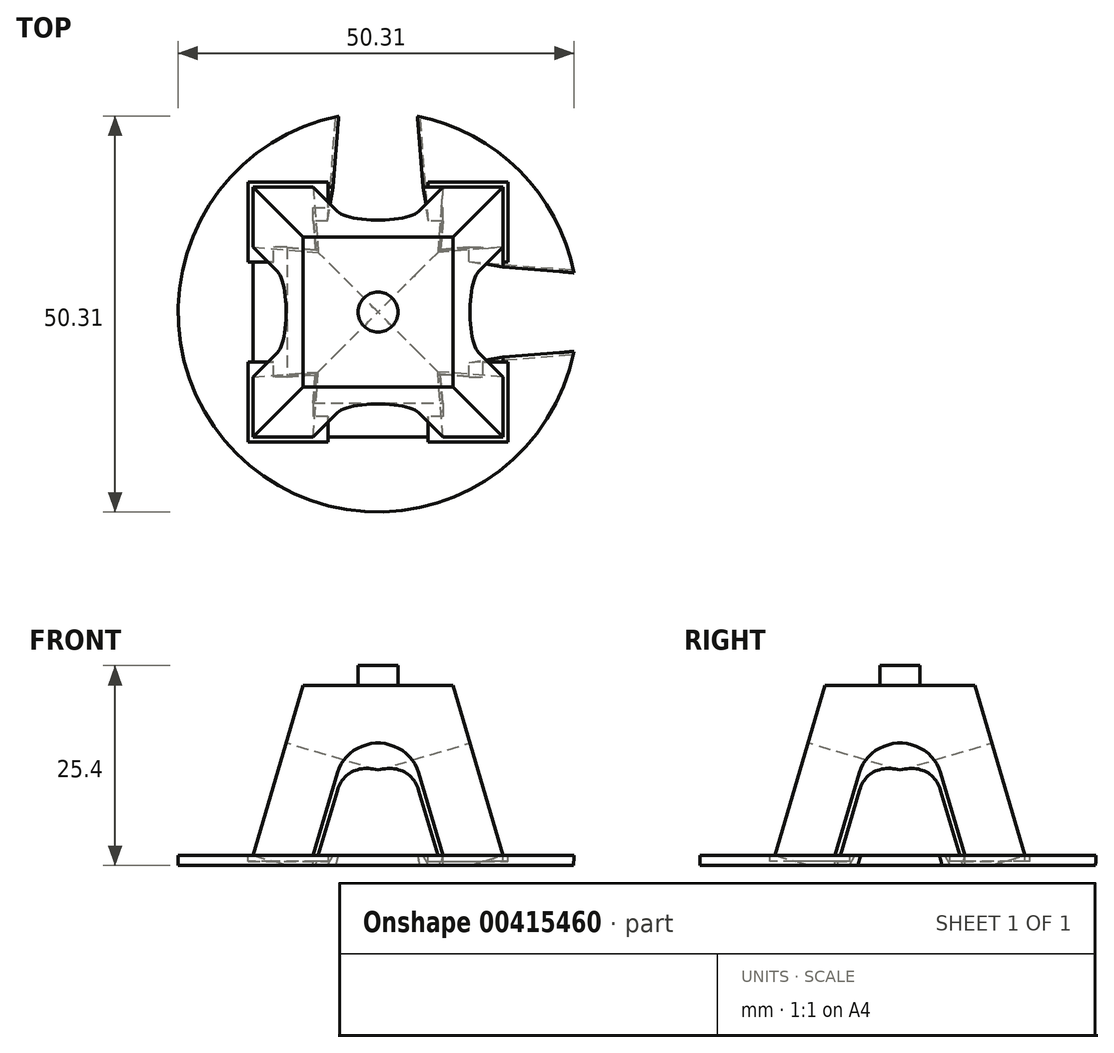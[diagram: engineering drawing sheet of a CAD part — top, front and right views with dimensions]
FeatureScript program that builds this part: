
annotation { "Feature Type Name" : "Feature", "Feature Type Description" : "" }
export const myFeature = defineFeature(function(context is Context, id is Id, definition is map)
    precondition{}
    {
        {
            var Q0;
            Q0=qCreatedBy(makeId("Top.planeOp"),FACE);
            var sketch = newSketch(context, id + "F0", { "sketchPlane" : qUnion([Q0])});
            skCircle(sketch, "E0", {"center": v(0, 0) * mm, "radius": 25.4 * mm});
            skSolve(sketch);
        }
        {
            var Q0;
            Q0=makeQuery(id+"F0.imprint","IMPRINT",FACE,{"disambiguationData":[TD([[makeQuery(id+"F0.imprint","IMPRINT",EDGE,{"derivedFrom":sQuery(id+"F0.wireOp",EDGE,"E0")}),1.0]])]});
            extrude(context, id + "F1", {"entities" : qUnion([Q0]), "oppositeDirection" : true, "depth" : 1.27 * mm});
        }
        {
            var Q0;
            Q0=qCreatedBy(makeId("Top.planeOp"),FACE);
            var sketch = newSketch(context, id + "F2", { "sketchPlane" : qUnion([Q0])});
            skLineSegment(sketch, "E1.bottom", {"start": v(-15.87, 15.88) * mm, "end": v(15.88, 15.88) * mm});
            skLineSegment(sketch, "E1.top", {"start": v(-15.88, -15.87) * mm, "end": v(15.87, -15.87) * mm});
            skLineSegment(sketch, "E1.left", {"start": v(-15.87, 15.88) * mm, "end": v(-15.88, -15.87) * mm});
            skLineSegment(sketch, "E1.right", {"start": v(15.88, 15.88) * mm, "end": v(15.87, -15.87) * mm});
            skPoint(sketch, "E1.middle", {"position": v(0, 0) * mm});
            skSolve(sketch);
        }
        {
            var Q0;
            Q0=qCreatedBy(makeId("Top.planeOp"),FACE);
            cPlane(context, id + "F3", {"entities" : qUnion([Q0]), "cplaneType" : CPlaneType.OFFSET, "offset" : 21.59 * mm, "width" : 152.4 * mm, "height" : 152.4 * mm});
        }
        {
            var Q0;
            Q0=qCreatedBy(id+"F3.planeOp",FACE);
            var sketch = newSketch(context, id + "F4", { "sketchPlane" : qUnion([Q0])});
            skLineSegment(sketch, "E2.bottom", {"start": v(-9.52, 9.53) * mm, "end": v(9.53, 9.53) * mm});
            skLineSegment(sketch, "E2.top", {"start": v(-9.53, -9.52) * mm, "end": v(9.52, -9.52) * mm});
            skLineSegment(sketch, "E2.left", {"start": v(-9.52, 9.53) * mm, "end": v(-9.53, -9.52) * mm});
            skLineSegment(sketch, "E2.right", {"start": v(9.53, 9.53) * mm, "end": v(9.53, -9.52) * mm});
            skPoint(sketch, "E2.middle", {"position": v(0, 0) * mm});
            skSolve(sketch);
        }
        {
            var Q1;
            Q1=makeQuery(id+"F2.imprint","IMPRINT",FACE,{"disambiguationData":[TD([[makeQuery(id+"F2.imprint","IMPRINT",EDGE,{"derivedFrom":sQuery(id+"F2.wireOp",EDGE,"E1.bottom")}),-1.0]])]});
            var Q2;
            Q2=makeQuery(id+"F4.imprint","IMPRINT",FACE,{"disambiguationData":[TD([[makeQuery(id+"F4.imprint","IMPRINT",EDGE,{"derivedFrom":sQuery(id+"F4.wireOp",EDGE,"E2.bottom")}),-1.0]])]});
            loft(context, id + "F5", {"sheetProfilesArray" : [{ "sheetProfileEntities" : qUnion([Q1]) }, { "sheetProfileEntities" : qUnion([Q2]) }]});
        }
        {
            var Q0;
            Q0=makeQuery(id+"F5.opLoft","SWEPT_FACE",FACE,{"disambiguationData":[OSD([sQuery(id+"F2.wireOp",EDGE,"E1.top"),sQuery(id+"F2.wireOp",EDGE,"E1.left"),sQuery(id+"F2.wireOp",EDGE,"E1.right"),sQuery(id+"F4.wireOp",EDGE,"E2.top"),sQuery(id+"F4.wireOp",EDGE,"E2.left"),sQuery(id+"F4.wireOp",EDGE,"E2.right")])]});
            var sketch = newSketch(context, id + "F6", { "sketchPlane" : qUnion([Q0])});
            skLineSegment(sketch, "E3.0.0", {"start": v(15.87, -4.48) * mm, "end": v(9.53, 18.03) * mm});
            skLineSegment(sketch, "E3.0.1", {"start": v(9.53, 18.03) * mm, "end": v(-9.53, 18.03) * mm});
            skLineSegment(sketch, "E3.0.2", {"start": v(-9.53, 18.03) * mm, "end": v(-15.88, -4.48) * mm});
            skLineSegment(sketch, "E3.0.3", {"start": v(-15.88, -4.48) * mm, "end": v(15.87, -4.48) * mm});
            skLineSegment(sketch, "E4", {"start": v(-8.26, -4.48) * mm, "end": v(-5.16, 6.5) * mm});
            skLineSegment(sketch, "E5", {"start": v(8.25, -4.48) * mm, "end": v(5.16, 6.5) * mm});
            skArc(sketch, "E6", {"start": v(5.16, 6.5) * mm, "mid": v(0, 10.4) * mm, "end": v(-5.16, 6.5) * mm});
            skLineSegment(sketch, "E7", {"start": v(-5.16, 6.5) * mm, "end": v(-1.9, 18.03) * mm, "construction": true});
            skLineSegment(sketch, "E8", {"start": v(5.16, 6.5) * mm, "end": v(1.9, 18.03) * mm, "construction": true});
            skSolve(sketch);
        }
        {
            var Q0;
            Q0=makeQuery(id+"F5.opLoft","SWEPT_FACE",FACE,{"disambiguationData":[OSD([sQuery(id+"F2.wireOp",EDGE,"E1.bottom"),sQuery(id+"F2.wireOp",EDGE,"E1.top"),sQuery(id+"F2.wireOp",EDGE,"E1.right"),sQuery(id+"F4.wireOp",EDGE,"E2.bottom"),sQuery(id+"F4.wireOp",EDGE,"E2.top"),sQuery(id+"F4.wireOp",EDGE,"E2.right")])]});
            var sketch = newSketch(context, id + "F7", { "sketchPlane" : qUnion([Q0])});
            skLineSegment(sketch, "E9.0.0", {"start": v(15.88, -4.48) * mm, "end": v(9.52, 18.03) * mm});
            skLineSegment(sketch, "E9.0.1", {"start": v(-9.52, 18.03) * mm, "end": v(9.53, 18.03) * mm});
            skLineSegment(sketch, "E9.0.2", {"start": v(-9.52, 18.03) * mm, "end": v(-15.87, -4.48) * mm});
            skLineSegment(sketch, "E9.0.3", {"start": v(-15.87, -4.48) * mm, "end": v(15.88, -4.48) * mm});
            skLineSegment(sketch, "E10", {"start": v(-8.25, -4.48) * mm, "end": v(-5.16, 6.5) * mm});
            skLineSegment(sketch, "E11", {"start": v(8.26, -4.48) * mm, "end": v(5.16, 6.5) * mm});
            skArc(sketch, "E12", {"start": v(5.16, 6.5) * mm, "mid": v(0, 10.4) * mm, "end": v(-5.16, 6.5) * mm});
            skSolve(sketch);
        }
        {
            var Q0;
            Q0=makeQuery(id+"F5.opLoft","SWEPT_FACE",FACE,{"disambiguationData":[OSD([sQuery(id+"F2.wireOp",EDGE,"E1.bottom"),sQuery(id+"F2.wireOp",EDGE,"E1.left"),sQuery(id+"F2.wireOp",EDGE,"E1.right"),sQuery(id+"F4.wireOp",EDGE,"E2.bottom"),sQuery(id+"F4.wireOp",EDGE,"E2.left"),sQuery(id+"F4.wireOp",EDGE,"E2.right")])]});
            var sketch = newSketch(context, id + "F8", { "sketchPlane" : qUnion([Q0])});
            skLineSegment(sketch, "E13.0.0", {"start": v(-9.53, 18.03) * mm, "end": v(9.52, 18.03) * mm});
            skLineSegment(sketch, "E13.0.1", {"start": v(-9.53, 18.03) * mm, "end": v(-15.88, -4.48) * mm});
            skLineSegment(sketch, "E13.0.2", {"start": v(-15.88, -4.48) * mm, "end": v(15.87, -4.48) * mm});
            skLineSegment(sketch, "E13.0.3", {"start": v(15.87, -4.48) * mm, "end": v(9.53, 18.03) * mm});
            skLineSegment(sketch, "E14", {"start": v(-8.26, -4.48) * mm, "end": v(-5.16, 6.5) * mm});
            skLineSegment(sketch, "E15", {"start": v(8.25, -4.48) * mm, "end": v(5.16, 6.5) * mm});
            skArc(sketch, "E16", {"start": v(5.16, 6.5) * mm, "mid": v(0, 10.4) * mm, "end": v(-5.16, 6.5) * mm});
            skSolve(sketch);
        }
        {
            var Q0;
            Q0=makeQuery(id+"F5.opLoft","SWEPT_FACE",FACE,{"disambiguationData":[OSD([sQuery(id+"F2.wireOp",EDGE,"E1.bottom"),sQuery(id+"F2.wireOp",EDGE,"E1.top"),sQuery(id+"F2.wireOp",EDGE,"E1.left"),sQuery(id+"F4.wireOp",EDGE,"E2.bottom"),sQuery(id+"F4.wireOp",EDGE,"E2.top"),sQuery(id+"F4.wireOp",EDGE,"E2.left")])]});
            var sketch = newSketch(context, id + "F9", { "sketchPlane" : qUnion([Q0])});
            skLineSegment(sketch, "E17.0.0", {"start": v(15.88, -4.48) * mm, "end": v(9.53, 18.03) * mm});
            skLineSegment(sketch, "E17.0.1", {"start": v(9.53, 18.03) * mm, "end": v(-9.52, 18.03) * mm});
            skLineSegment(sketch, "E17.0.2", {"start": v(-9.53, 18.03) * mm, "end": v(-15.87, -4.48) * mm});
            skLineSegment(sketch, "E17.0.3", {"start": v(-15.87, -4.48) * mm, "end": v(15.88, -4.48) * mm});
            skLineSegment(sketch, "E18", {"start": v(-8.25, -4.48) * mm, "end": v(-5.16, 6.5) * mm});
            skLineSegment(sketch, "E19", {"start": v(8.26, -4.48) * mm, "end": v(5.16, 6.5) * mm});
            skArc(sketch, "E20", {"start": v(5.16, 6.5) * mm, "mid": v(0, 10.4) * mm, "end": v(-5.16, 6.5) * mm});
            skSolve(sketch);
        }
        {
            var Q0;
            {var subQ0=sQuery(id+"F9.wireOp",EDGE,"E18");Q0=makeQuery(id+"F9.imprint","IMPRINT",FACE,{"disambiguationData":[TD([[makeQuery(id+"F9.imprint","IMPRINT",EDGE,{"derivedFrom":subQ0}),-1.0]])]});}
            extrude(context, id + "F10", {"entities" : qUnion([Q0]), "operationType" : NewBodyOperationType.REMOVE, "oppositeDirection" : true, "depth" : 74.42 * mm});
        }
        {
            var Q0;
            {var subQ0=sQuery(id+"F6.wireOp",EDGE,"E4");Q0=makeQuery(id+"F6.imprint","IMPRINT",FACE,{"disambiguationData":[TD([[makeQuery(id+"F6.imprint","IMPRINT",EDGE,{"derivedFrom":subQ0}),-1.0]])]});}
            extrude(context, id + "F11", {"entities" : qUnion([Q0]), "operationType" : NewBodyOperationType.REMOVE, "oppositeDirection" : true, "depth" : 67.8 * mm});
        }
        {
            var Q0;
            {var subQ0=sQuery(id+"F7.wireOp",EDGE,"E10");Q0=makeQuery(id+"F7.imprint","IMPRINT",FACE,{"disambiguationData":[TD([[makeQuery(id+"F7.imprint","IMPRINT",EDGE,{"derivedFrom":subQ0}),-1.0]])]});}
            extrude(context, id + "F12", {"entities" : qUnion([Q0]), "operationType" : NewBodyOperationType.REMOVE, "oppositeDirection" : true, "depth" : 25.4 * mm});
        }
        {
            var Q0;
            {var subQ0=sQuery(id+"F8.wireOp",EDGE,"E14");Q0=makeQuery(id+"F8.imprint","IMPRINT",FACE,{"disambiguationData":[TD([[makeQuery(id+"F8.imprint","IMPRINT",EDGE,{"derivedFrom":subQ0}),-1.0]])]});}
            extrude(context, id + "F13", {"entities" : qUnion([Q0]), "operationType" : NewBodyOperationType.REMOVE, "oppositeDirection" : true, "depth" : 25.4 * mm});
        }
        {
            var Q0;
            Q0=makeQuery(id+"F1.opExtrude","CAP_FACE",FACE,{"disambiguationData":[OSD([sQuery(id+"F0.wireOp",EDGE,"E0")])],"isStart":true});
            var sketch = newSketch(context, id + "F14", { "sketchPlane" : qUnion([Q0])});
            skCircle(sketch, "E21.0.0", {"center": v(0, 0) * mm, "radius": 25.4 * mm});
            skLineSegment(sketch, "E22.bottom", {"start": v(-16.51, 16.51) * mm, "end": v(16.5, 16.51) * mm});
            skLineSegment(sketch, "E22.top", {"start": v(-16.5, -16.51) * mm, "end": v(16.51, -16.51) * mm});
            skLineSegment(sketch, "E22.left", {"start": v(-16.51, 16.5) * mm, "end": v(-16.5, -16.51) * mm});
            skLineSegment(sketch, "E22.right", {"start": v(16.5, 16.51) * mm, "end": v(16.51, -16.51) * mm});
            skLineSegment(sketch, "E23", {"start": v(0, 0) * mm, "end": v(0, 25.4) * mm, "construction": true});
            skLineSegment(sketch, "E24", {"start": v(0, 0) * mm, "end": v(25.4, 0) * mm, "construction": true});
            skLineSegment(sketch, "E25", {"start": v(-6.35, 24.6) * mm, "end": v(-6.35, -24.6) * mm});
            skLineSegment(sketch, "E26", {"start": v(6.35, 24.6) * mm, "end": v(6.35, -24.6) * mm});
            skLineSegment(sketch, "E27", {"start": v(-24.6, -6.35) * mm, "end": v(24.6, -6.35) * mm});
            skLineSegment(sketch, "E28", {"start": v(24.6, 6.35) * mm, "end": v(-24.6, 6.35) * mm});
            skSolve(sketch);
        }
        {
            var Q0;
            {var subQ0=sQuery(id+"F14.wireOp",EDGE,"E22.right");var subQ1=sQuery(id+"F14.wireOp",EDGE,"E22.bottom");var subQ2=makeQuery(id+"F14.imprint","INTERSECT",VERTEX,{"derivedFrom":[subQ1,subQ0]});Q0=makeQuery(id+"F14.imprint","IMPRINT",FACE,{"disambiguationData":[TD([[makeQuery(id+"F14.imprint","IMPRINT",EDGE,{"disambiguationData":[TD([[subQ2,1.0]])],"derivedFrom":subQ1}),-1.0]])]});}
            var Q1;
            {var subQ0=sQuery(id+"F14.wireOp",EDGE,"E22.right");var subQ1=sQuery(id+"F14.wireOp",EDGE,"E22.top");var subQ2=makeQuery(id+"F14.imprint","INTERSECT",VERTEX,{"derivedFrom":[subQ1,subQ0]});Q1=makeQuery(id+"F14.imprint","IMPRINT",FACE,{"disambiguationData":[TD([[makeQuery(id+"F14.imprint","IMPRINT",EDGE,{"disambiguationData":[TD([[subQ2,1.0]])],"derivedFrom":subQ1}),1.0]])]});}
            var Q2;
            {var subQ0=sQuery(id+"F14.wireOp",EDGE,"E22.left");var subQ1=sQuery(id+"F14.wireOp",EDGE,"E22.bottom");var subQ2=makeQuery(id+"F14.imprint","INTERSECT",VERTEX,{"derivedFrom":[subQ1,subQ0]});Q2=makeQuery(id+"F14.imprint","IMPRINT",FACE,{"disambiguationData":[TD([[makeQuery(id+"F14.imprint","IMPRINT",EDGE,{"disambiguationData":[TD([[subQ2,-1.0]])],"derivedFrom":subQ1}),-1.0]])]});}
            var Q3;
            {var subQ0=sQuery(id+"F14.wireOp",EDGE,"E22.left");var subQ1=sQuery(id+"F14.wireOp",EDGE,"E22.top");var subQ2=makeQuery(id+"F14.imprint","INTERSECT",VERTEX,{"derivedFrom":[subQ1,subQ0]});Q3=makeQuery(id+"F14.imprint","IMPRINT",FACE,{"disambiguationData":[TD([[makeQuery(id+"F14.imprint","IMPRINT",EDGE,{"disambiguationData":[TD([[subQ2,-1.0]])],"derivedFrom":subQ1}),1.0]])]});}
            extrude(context, id + "F15", {"entities" : qUnion([Q0, Q1, Q2, Q3]), "operationType" : NewBodyOperationType.REMOVE, "oppositeDirection" : true, "depth" : 0.76 * mm});
        }
        {
            var Q0;
            Q0=makeQuery(id+"F5.opLoft","CAP_FACE",FACE,{"disambiguationData":[OSD([makeQuery(id+"F4.imprint","IMPRINT",FACE,{"disambiguationData":[TD([[makeQuery(id+"F4.imprint","IMPRINT",EDGE,{"derivedFrom":sQuery(id+"F4.wireOp",EDGE,"E2.bottom")}),-1.0]])]})])],"isStart":true});
            var sketch = newSketch(context, id + "F16", { "sketchPlane" : qUnion([Q0])});
            skCircle(sketch, "E29", {"center": v(0, 0) * mm, "radius": 2.54 * mm});
            skSolve(sketch);
        }
        {
            var Q0;
            Q0=makeQuery(id+"F16.imprint","IMPRINT",FACE,{"disambiguationData":[TD([[makeQuery(id+"F16.imprint","IMPRINT",EDGE,{"derivedFrom":sQuery(id+"F16.wireOp",EDGE,"E29")}),1.0]])]});
            extrude(context, id + "F17", {"entities" : qUnion([Q0]), "operationType" : NewBodyOperationType.ADD, "depth" : 2.54 * mm});
        }
        {
            var Q0;
            Q0=makeQuery(id+"F1.opExtrude","CAP_FACE",FACE,{"disambiguationData":[OSD([sQuery(id+"F0.wireOp",EDGE,"E0")])],"isStart":true});
            var sketch = newSketch(context, id + "F18", { "sketchPlane" : qUnion([Q0])});
            skCircle(sketch, "E30", {"center": v(0, 0) * mm, "radius": 3.43 * mm});
            skSolve(sketch);
        }
        {
            var Q0;
            Q0=makeQuery(id+"F18.imprint","IMPRINT",FACE,{"disambiguationData":[TD([[makeQuery(id+"F18.imprint","IMPRINT",EDGE,{"derivedFrom":sQuery(id+"F18.wireOp",EDGE,"E30")}),1.0]])]});
            extrude(context, id + "F19", {"entities" : qUnion([Q0]), "operationType" : NewBodyOperationType.REMOVE, "oppositeDirection" : true, "depth" : 25.4 * mm});
        }
    });
